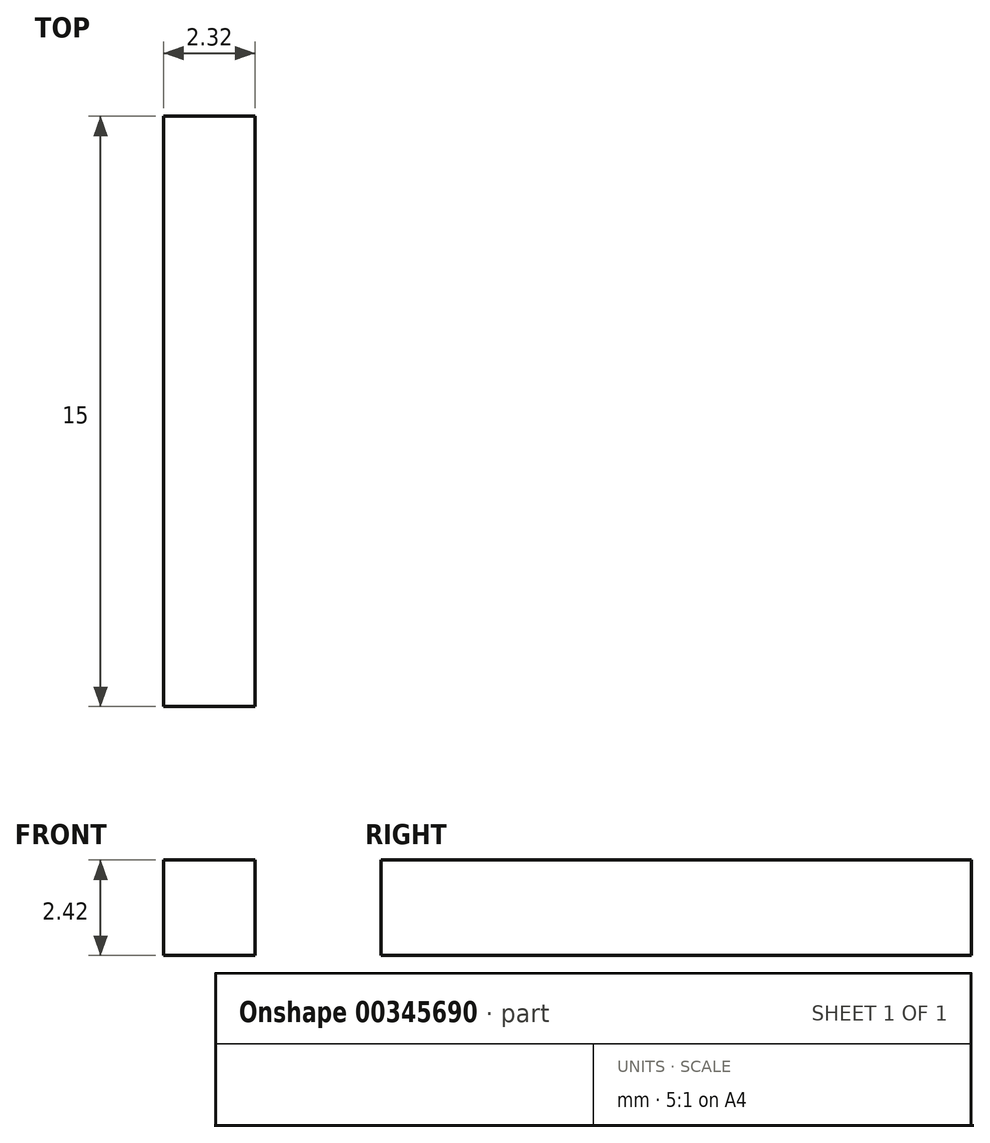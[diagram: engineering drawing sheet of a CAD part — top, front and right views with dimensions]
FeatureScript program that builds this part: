
annotation { "Feature Type Name" : "Feature", "Feature Type Description" : "" }
export const myFeature = defineFeature(function(context is Context, id is Id, definition is map)
    precondition{}
    {
        {
            var Q0;
            Q0=qCreatedBy(makeId("Front.planeOp"),FACE);
            var sketch = newSketch(context, id + "F0", { "sketchPlane" : qUnion([Q0])});
            skLineSegment(sketch, "E0.bottom", {"start": v(-0.49, 0) * mm, "end": v(1.83, 0) * mm});
            skLineSegment(sketch, "E0.top", {"start": v(-0.49, 2.42) * mm, "end": v(1.83, 2.42) * mm});
            skLineSegment(sketch, "E0.left", {"start": v(-0.49, 0) * mm, "end": v(-0.49, 2.42) * mm});
            skLineSegment(sketch, "E0.right", {"start": v(1.83, 0) * mm, "end": v(1.83, 2.42) * mm});
            skSolve(sketch);
        }
        {
            var Q0;
            Q0=makeQuery(id+"F0.imprint","IMPRINT",FACE,{"disambiguationData":[TD([[makeQuery(id+"F0.imprint","IMPRINT",EDGE,{"derivedFrom":sQuery(id+"F0.wireOp",EDGE,"E0.bottom")}),1.0]])]});
            extrude(context, id + "F1", {"entities" : qUnion([Q0]), "depth" : 15 * mm});
        }
    });
